# Revit family: Haworth_Haworth_Soji_Chair_Task_XL_NA
name_source: partatom
category: Furniture
units: mm (PartAtom-declared; Revit-internal decimal feet)

## family parameters
Always vertical = Yes
Cut with Voids When Loaded = No
OmniClass Number = 23.40.70.14.64.11
OmniClass Title = Office Furniture
Room Calculation Point = No
Shared = No
Work Plane-Based = No

## types (6) — shared parameters
Actual Depth = 28 "
Actual Width = 34 "
Assembly Code = E2020200
Caster Finish = Haworth _ Polymer _ Black
Hardware Finish = Haworth _ Polymer _ Undecided
Lumbar Finish = Haworth _ Polymer _ Undecided
Manufacturer = Haworth
Model = Haworth Soji Chair Task XL
Product URL = https://www.haworth.com
Revision Number = 1
Support Finish = Haworth _ Metal _ Undecided
URL = https://www.haworth.com
Warranty = https://www.haworth.com

## per-type parameters (varying)
| type | Arms | Description | Fixed Arms | Height Adjustable Arms | With Lumbar | Without Arms | Without Lumbar |
| Height Adjustable Arms - With Lumbar | Yes | Haworth Soji Chair Task XL - Height Adjustable Arms - With Lumbar | No | Yes | Yes | No | No |
| Height Adjustable Arms - Without Lumbar | Yes | Haworth Soji Chair Task XL - Height Adjustable Arms - Without Lumbar | No | Yes | No | No | Yes |
| Fixed Arms - With Lumbar | Yes | Haworth Soji Chair Task XL - Fixed Arms - With Lumbar | Yes | No | Yes | No | No |
| Fixed Arms - Without Lumbar | Yes | Haworth Soji Chair Task XL - Fixed Arms - Without Lumbar | Yes | No | No | No | Yes |
| Without Arms - With Lumbar | No | Haworth Soji Chair Task XL - Without Arms - With Lumbar | No | No | Yes | Yes | No |
| Without Arms - Without Lumbar | No | Haworth Soji Chair Task XL - Without Arms - Without Lumbar | No | No | No | Yes | Yes |

## geometry (parser evidence)
native form markers: Sweep x22
no freeform markers — native parametric forms only
